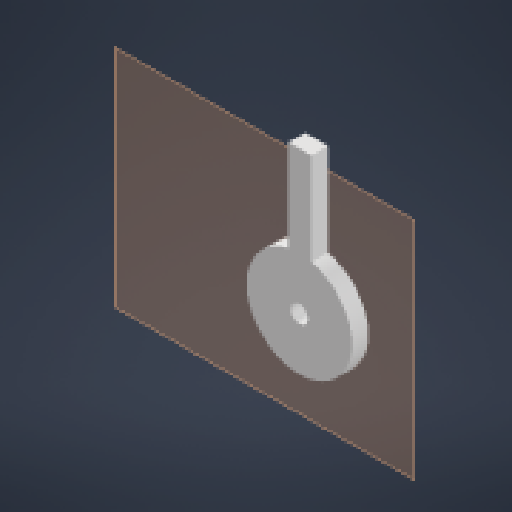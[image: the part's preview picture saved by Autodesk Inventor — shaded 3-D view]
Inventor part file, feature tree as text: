
AUTODESK INVENTOR PART (.ipt)
format: ipt  version: 2023 (Build 270158000, 158)  size: 131,584 bytes
history: native  units: in
note: dims shown in document units (in); Inventor stores cm internally (conversion verified against a paired STEP export)
features: other x4, reference x3, plane x2, sketch x1, extrude x1
ambient origin geometry x8: Origin, YZ Plane, XZ Plane, XY Plane, X Axis, Y Axis, Z Axis, Center Point
bodies: Solid1 (feature_tree)
feature tree (11):
  plane  "Work Plane1"
  sketch  "Sketch1"  dims[d0=1.154in d2=1.0in d3=90.0deg d4=0.125in d5=0.0in d6=0.125in d7=0.577in d8=1.0in d9=0.0in]
  plane  "Work Plane2"
  extrude  "Extrusion1"  Depth=0.577in
  reference  "Reference1"
  reference  "Reference2"
  reference  "Reference3"
  parser-record x1  (decoder bookkeeping rows leaked as tree rows — omitted from the tree; the rows remain in map.json)
  other  "Gripper.iam"
  other  "Base:1"
  other  "Servo:1"
note: 1 file-system path scrubbed to <path> (originals preserved in map.json)
